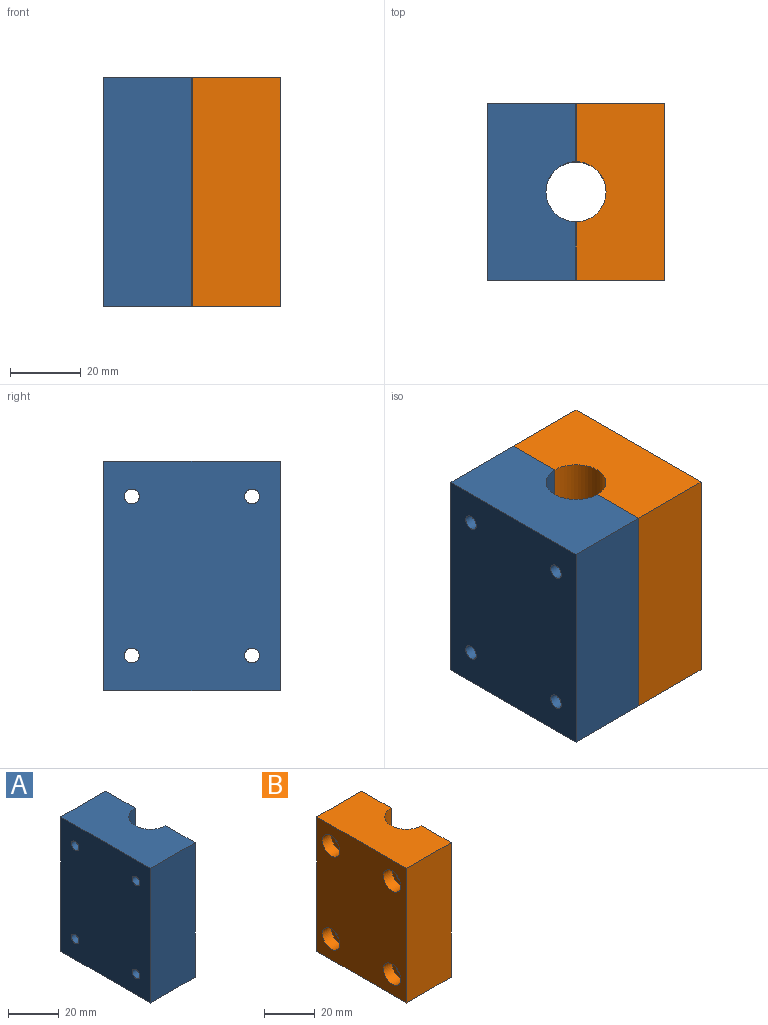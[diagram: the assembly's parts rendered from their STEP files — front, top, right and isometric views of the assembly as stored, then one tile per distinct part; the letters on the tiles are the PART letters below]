
ASSEMBLY  parts=2 mates=1
PART A: 12 faces, bbox 25x50x65 mm
  f0: plane 65x16.5mm, normal (1,0,0), area 1044.8mm2, adj f2,f5,f6,f7,f10,f11
  f1: plane 65x50mm, normal (-1,0,0), area 3194.6mm2, adj f2,f4,f5,f6,f8,f9,f10,f11
  f2: plane 65x25mm, normal (0,-1,0), area 1625mm2, adj f0,f1,f5,f6
  f3: plane 65x16.5mm, normal (1,0,0), area 1044.8mm2, adj f4,f5,f6,f7,f8,f9
  f4: plane 65x25mm, normal (0,1,0), area 1625mm2, adj f1,f3,f5,f6
  f5: plane 50x25mm, normal (0,0,1), area 1136.5mm2, adj f0,f1,f2,f3,f4,f7
  f6: plane 50x25mm, normal (0,0,-1), area 1136.5mm2, adj f0,f1,f2,f3,f4,f7
  f7: cylinder r=8.5mm len=65mm, axis (0,0,1), area 1735.7mm2, adj f0,f3,f5,f6
  f8: cylinder r=2.1mm len=25mm, axis (1,0,0), area 329.9mm2, adj f1,f3
  f9: cylinder r=2.1mm len=25mm, axis (1,0,0), area 329.9mm2, adj f1,f3
  f10: cylinder r=2.1mm len=25mm, axis (1,0,0), area 329.9mm2, adj f0,f1
  f11: cylinder r=2.1mm len=25mm, axis (1,0,0), area 329.9mm2, adj f0,f1
PART B: 20 faces, bbox 25x50x65 mm
  f0: plane 65x16.5mm, normal (1,0,0), area 1025mm2, adj f2,f5,f6,f7,f14,f17
  f1: plane 65x50mm, normal (-1,0,0), area 2951.4mm2, adj f2,f4,f5,f6,f10,f13,f16,f19
  f2: plane 65x25mm, normal (0,-1,0), area 1625mm2, adj f0,f1,f5,f6
  f3: plane 65x16.5mm, normal (1,0,0), area 1025mm2, adj f4,f5,f6,f7,f8,f11
  f4: plane 65x25mm, normal (0,1,0), area 1625mm2, adj f1,f3,f5,f6
  f5: plane 50x25mm, normal (0,0,1), area 1136.5mm2, adj f0,f1,f2,f3,f4,f7
  f6: plane 50x25mm, normal (0,0,-1), area 1136.5mm2, adj f0,f1,f2,f3,f4,f7
  f7: cylinder r=8.5mm len=65mm, axis (0,0,1), area 1735.7mm2, adj f0,f3,f5,f6
  f8: cylinder r=2.75mm len=20mm, axis (-1,0,0), area 345.6mm2, adj f3,f9
  f9: plane 9.75x9.75mm, normal (-1,0,0), area 50.9mm2, adj f8,f10
  f10: cylinder r=4.88mm len=9.75mm, axis (-1,0,0), area 153.2mm2, adj f1,f9
  f11: cylinder r=2.75mm len=20mm, axis (-1,0,0), area 345.6mm2, adj f3,f12
  f12: plane 9.75x9.75mm, normal (-1,0,0), area 50.9mm2, adj f11,f13
  f13: cylinder r=4.88mm len=9.75mm, axis (-1,0,0), area 153.2mm2, adj f1,f12
  f14: cylinder r=2.75mm len=20mm, axis (-1,0,0), area 345.6mm2, adj f0,f15
  f15: plane 9.75x9.75mm, normal (-1,0,0), area 50.9mm2, adj f14,f16
  f16: cylinder r=4.88mm len=9.75mm, axis (-1,0,0), area 153.2mm2, adj f1,f15
  f17: cylinder r=2.75mm len=20mm, axis (-1,0,0), area 345.6mm2, adj f0,f18
  f18: plane 9.75x9.75mm, normal (-1,0,0), area 50.9mm2, adj f17,f19
  f19: cylinder r=4.88mm len=9.75mm, axis (-1,0,0), area 153.2mm2, adj f1,f18
PLACE A t=(-16.72,-29.15,12.01)mm
PLACE B rot(axis=(0,0,1),180deg) t=(33.28,20.85,12.01)mm
MATE cylindrical A.f9 <-> B.f14  axis (1,0,0) through (8.28,12.85,67.01)mm
